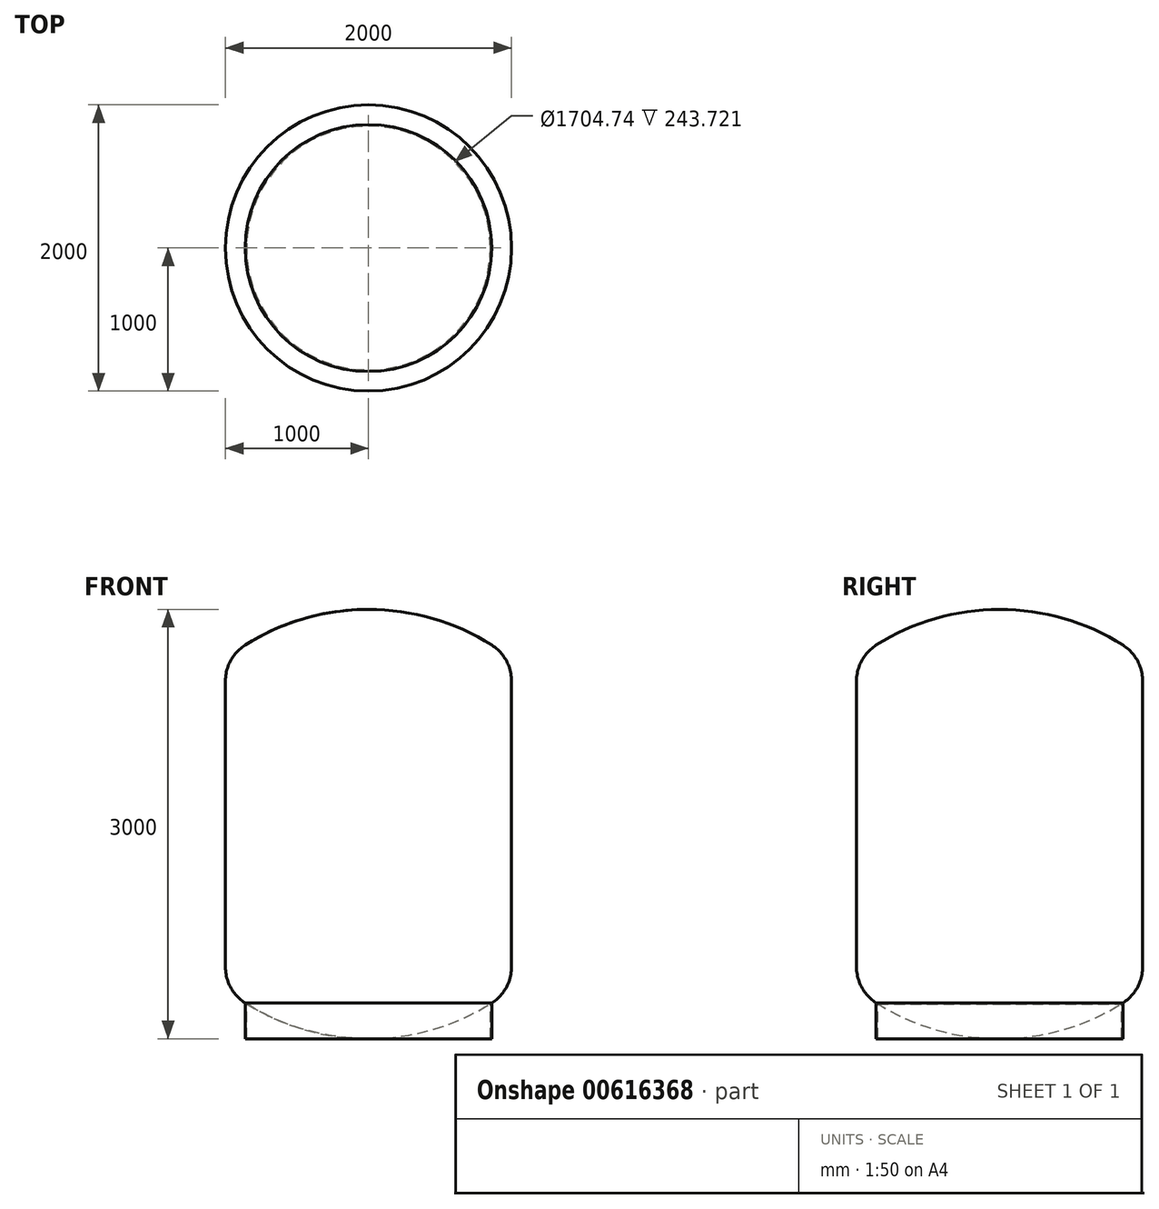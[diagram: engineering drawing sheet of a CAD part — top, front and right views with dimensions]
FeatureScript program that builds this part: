
annotation { "Feature Type Name" : "Feature", "Feature Type Description" : "" }
export const myFeature = defineFeature(function(context is Context, id is Id, definition is map)
    precondition{}
    {
        {
            var Q0;
            Q0=qCreatedBy(makeId("Front.planeOp"),FACE);
            var sketch = newSketch(context, id + "F0", { "sketchPlane" : qUnion([Q0])});
            skLineSegment(sketch, "E0.bottom", {"start": v(0, 0) * mm, "end": v(-1000, 0) * mm, "construction": true});
            skLineSegment(sketch, "E0.top", {"start": v(0, 1000) * mm, "end": v(-1000, 1000) * mm, "construction": true});
            skLineSegment(sketch, "E0.right", {"start": v(-1000, 0) * mm, "end": v(-1000, 1000) * mm});
            skArc(sketch, "E1", {"start": v(-1000, 1000) * mm, "mid": v(-963.32, 1142.69) * mm, "end": v(-862.37, 1250) * mm});
            skArc(sketch, "E2", {"start": v(-862.37, 1250) * mm, "mid": v(-448.94, 1436.24) * mm, "end": v(0, 1500) * mm});
            skLineSegment(sketch, "E3", {"start": v(0, 1500) * mm, "end": v(0, 0) * mm});
            skLineSegment(sketch, "E4.MirrorCS", {"start": v(0, -1500) * mm, "end": v(0, 0) * mm});
            skArc(sketch, "E5.MirrorCS", {"start": v(-862.37, -1250) * mm, "mid": v(-448.94, -1436.24) * mm, "end": v(0, -1500) * mm});
            skArc(sketch, "E6.MirrorCS", {"start": v(-1000, -1000) * mm, "mid": v(-963.32, -1142.69) * mm, "end": v(-862.37, -1250) * mm});
            skLineSegment(sketch, "E7.MirrorCS", {"start": v(0, -1000) * mm, "end": v(-1000, -1000) * mm, "construction": true});
            skLineSegment(sketch, "E8.MirrorCS", {"start": v(-1000, 0) * mm, "end": v(-1000, -1000) * mm});
            skSolve(sketch);
        }
        {
            var Q0;
            Q0=makeQuery(id+"F0.imprint","IMPRINT",FACE,{"disambiguationData":[TD([[makeQuery(id+"F0.imprint","IMPRINT",EDGE,{"derivedFrom":sQuery(id+"F0.wireOp",EDGE,"E0.right")}),-1.0]])]});
            var sketch = newSketch(context, id + "F1", { "sketchPlane" : qUnion([Q0])});
            skLineSegment(sketch, "E9", {"start": v(-862.37, -1250) * mm, "end": v(-862.37, -1500) * mm});
            skLineSegment(sketch, "E10", {"start": v(-862.37, -1500) * mm, "end": v(-852.37, -1500) * mm});
            skLineSegment(sketch, "E11", {"start": v(-852.37, -1500) * mm, "end": v(-852.37, -1256.28) * mm});
            skArc(sketch, "E12", {"start": v(-862.37, -1250) * mm, "mid": v(-857.38, -1253.15) * mm, "end": v(-852.37, -1256.28) * mm});
            skLineSegment(sketch, "E13", {"start": v(-862.37, -1500) * mm, "end": v(-862.37, 0) * mm, "construction": true});
            skSolve(sketch);
        }
        {
            var Q0;
            Q0 = qSketchRegion(id + "F0", true);
            var Q1;
            Q1 = qSketchRegion(id + "F1", true);
            var Q2;
            Q2=sQuery(id+"F0.wireOp",EDGE,"E3");
            revolve(context, id + "F2", {"entities" : qUnion([Q0, Q1]), "axis" : qUnion([Q2]), "revolveType" : RevolveType.FULL});
        }
    });
